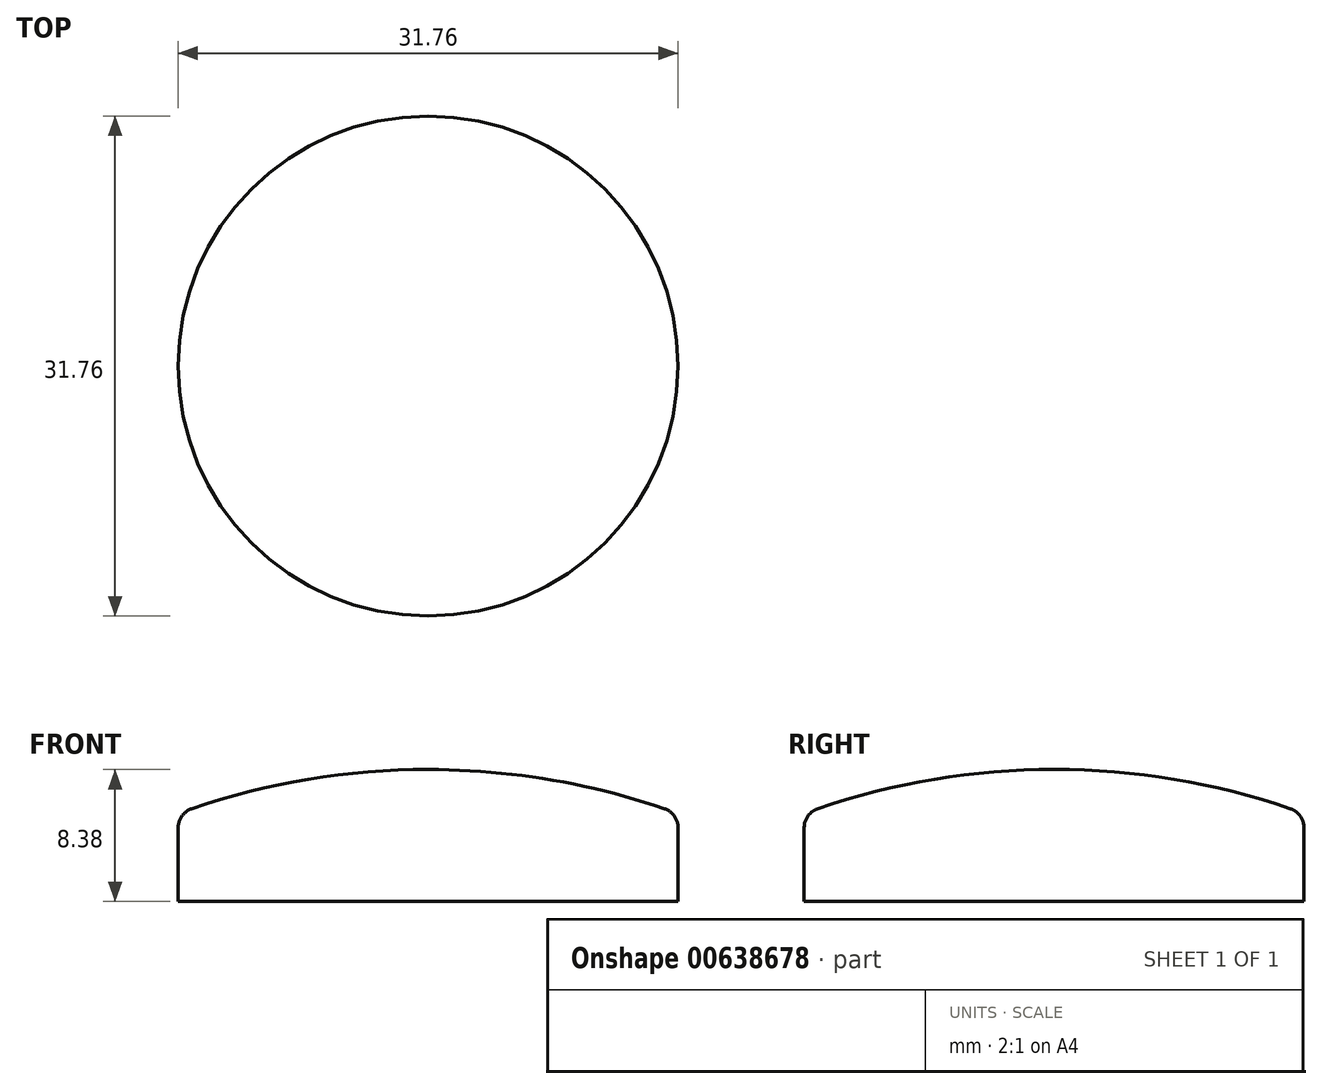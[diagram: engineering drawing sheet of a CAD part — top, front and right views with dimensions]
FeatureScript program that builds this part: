
annotation { "Feature Type Name" : "Feature", "Feature Type Description" : "" }
export const myFeature = defineFeature(function(context is Context, id is Id, definition is map)
    precondition{}
    {
        {
            var Q0;
            Q0=qCreatedBy(makeId("Front.planeOp"),FACE);
            var sketch = newSketch(context, id + "F0", { "sketchPlane" : qUnion([Q0])});
            skLineSegment(sketch, "E0.bottom", {"start": v(0, 0) * mm, "end": v(15.88, 0) * mm});
            skLineSegment(sketch, "E0.left", {"start": v(0, 0) * mm, "end": v(0, 8.38) * mm});
            skLineSegment(sketch, "E1", {"start": v(15.88, 5.59) * mm, "end": v(0, 5.59) * mm, "construction": true});
            skLineSegment(sketch, "E2", {"start": v(15.88, 0) * mm, "end": v(15.88, 5.59) * mm});
            skLineSegment(sketch, "E3", {"start": v(-15.88, 0) * mm, "end": v(-15.88, 5.59) * mm, "construction": true});
            skArc(sketch, "E4", {"start": v(15.88, 5.59) * mm, "mid": v(8.06, 7.68) * mm, "end": v(0, 8.38) * mm});
            skSolve(sketch);
        }
        {
            var Q0;
            Q0=makeQuery(id+"F0.imprint","IMPRINT",FACE,{"disambiguationData":[TD([[makeQuery(id+"F0.imprint","IMPRINT",EDGE,{"derivedFrom":sQuery(id+"F0.wireOp",EDGE,"E0.bottom")}),1.0]])]});
            var Q1;
            Q1=sQuery(id+"F0.wireOp",EDGE,"E0.left");
            revolve(context, id + "F1", {"entities" : qUnion([Q0]), "axis" : qUnion([Q1]), "revolveType" : RevolveType.FULL});
        }
        {
            var Q0;
            Q0=makeQuery(id+"F1.opRevolve","SWEPT_EDGE",EDGE,{"disambiguationData":[OSD([sQuery(id+"F0.wireOp",EDGE,"E2"),sQuery(id+"F0.wireOp",EDGE,"E4")])]});
            fillet(context, id + "F2", {"entities" : qUnion([Q0]), "radius" : 1.27 * mm, "tangentPropagation" : true, "allowEdgeOverflow" : false});
        }
    });
